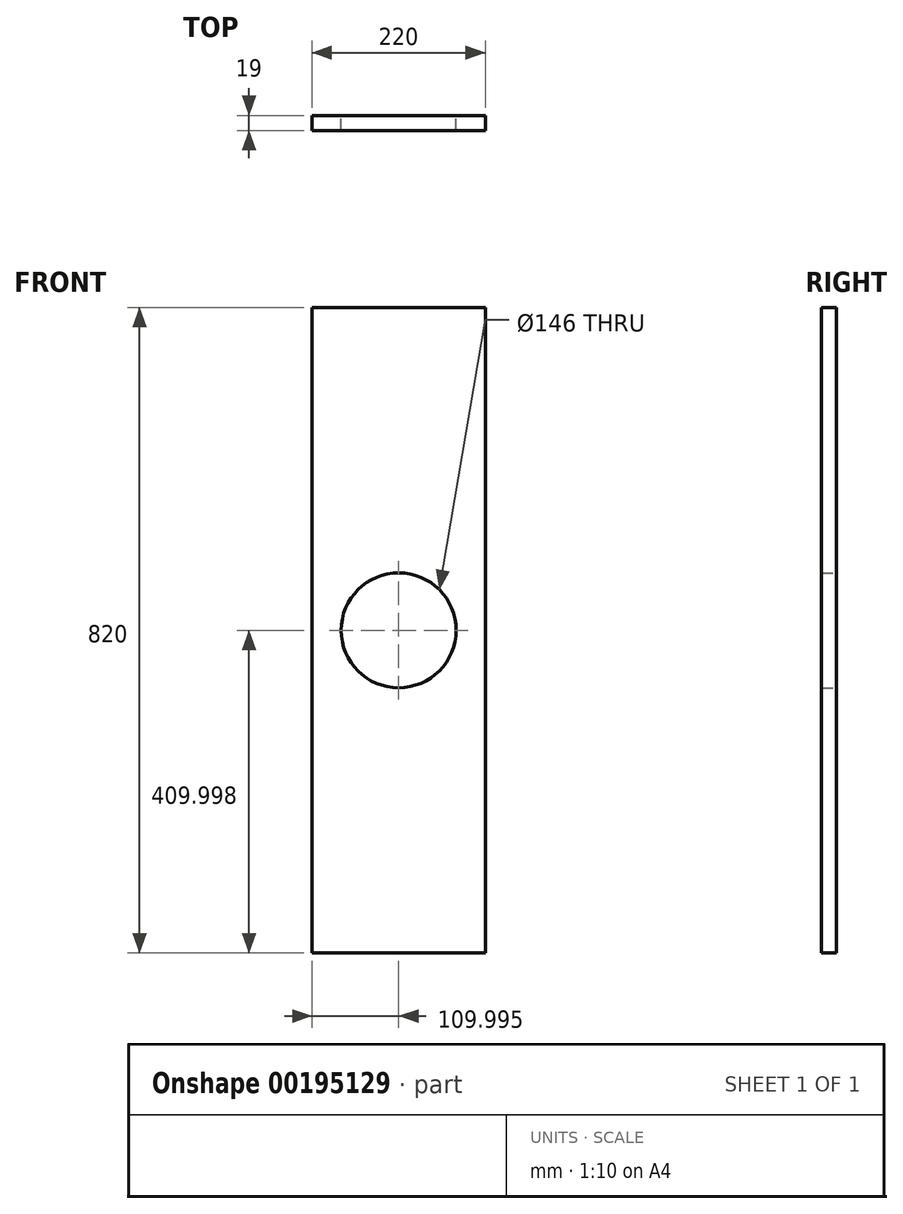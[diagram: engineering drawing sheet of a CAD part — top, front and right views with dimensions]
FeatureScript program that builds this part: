
annotation { "Feature Type Name" : "Feature", "Feature Type Description" : "" }
export const myFeature = defineFeature(function(context is Context, id is Id, definition is map)
    precondition{}
    {
        {
            var Q0;
            Q0=qCreatedBy(makeId("Front.planeOp"),FACE);
            var sketch = newSketch(context, id + "F0", { "sketchPlane" : qUnion([Q0])});
            skLineSegment(sketch, "E0.bottom", {"start": v(-168.94, 828.07) * mm, "end": v(51.06, 828.07) * mm});
            skLineSegment(sketch, "E0.top", {"start": v(-168.94, 8.07) * mm, "end": v(51.06, 8.07) * mm});
            skLineSegment(sketch, "E0.left", {"start": v(-168.94, 828.07) * mm, "end": v(-168.94, 8.07) * mm});
            skLineSegment(sketch, "E0.right", {"start": v(51.06, 828.07) * mm, "end": v(51.06, 8.07) * mm});
            skCircle(sketch, "E1", {"center": v(-58.94, 418.07) * mm, "radius": 73 * mm});
            skSolve(sketch);
        }
        {
            var Q0;
            Q0=makeQuery(id+"F0.imprint","IMPRINT",FACE,{"disambiguationData":[TD([[makeQuery(id+"F0.imprint","IMPRINT",EDGE,{"derivedFrom":sQuery(id+"F0.wireOp",EDGE,"E0.bottom")}),-1.0]])]});
            extrude(context, id + "F1", {"entities" : qUnion([Q0]), "depth" : 19 * mm});
        }
    });
